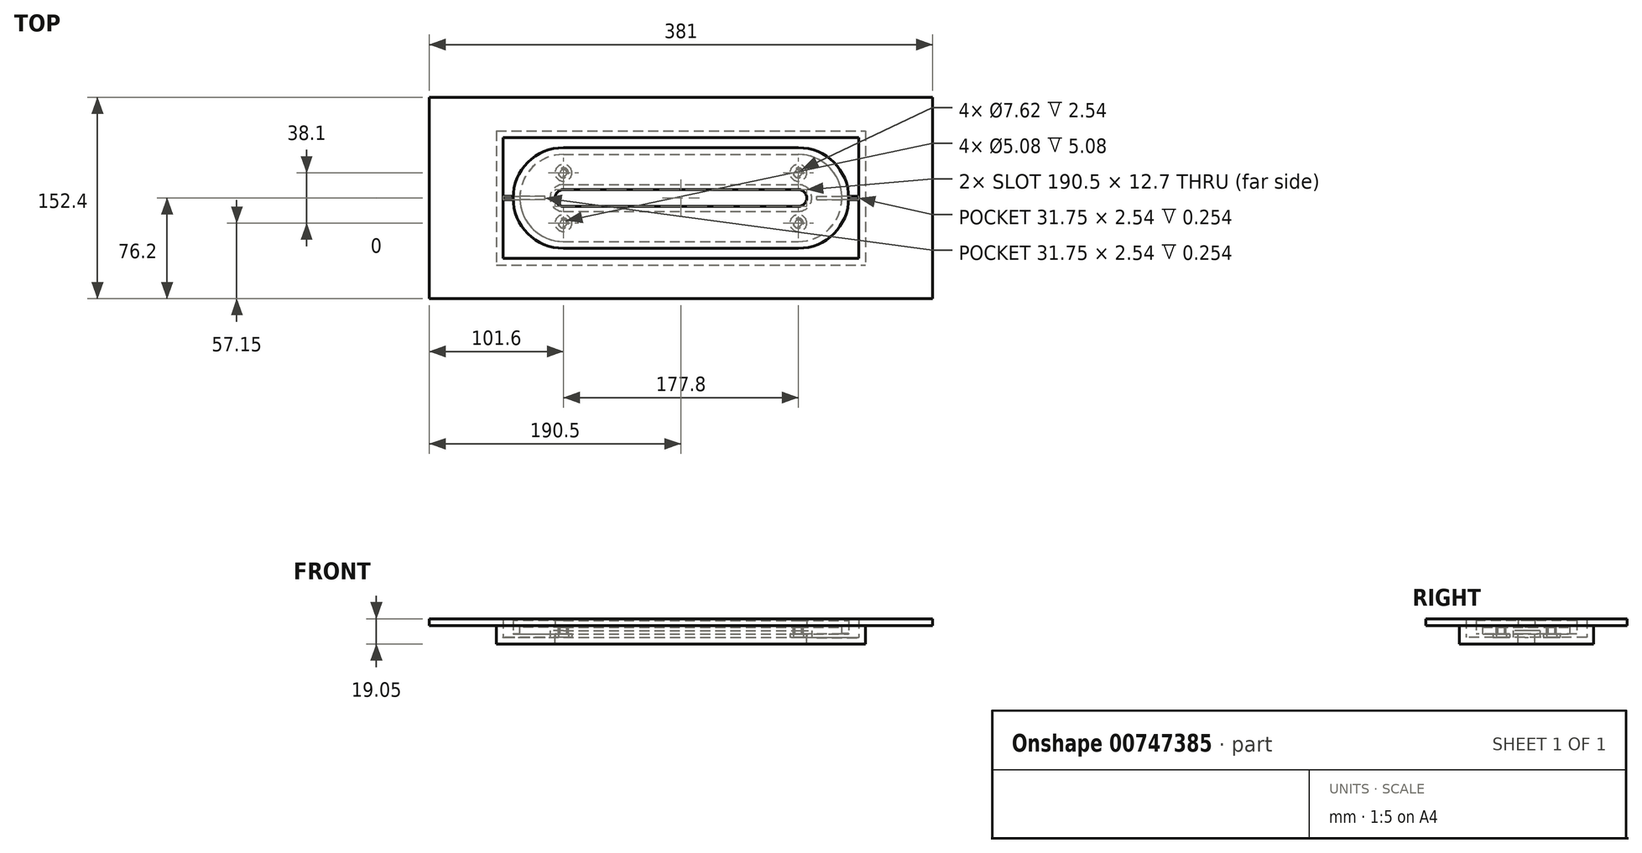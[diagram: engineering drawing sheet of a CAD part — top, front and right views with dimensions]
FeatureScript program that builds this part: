
annotation { "Feature Type Name" : "Feature", "Feature Type Description" : "" }
export const myFeature = defineFeature(function(context is Context, id is Id, definition is map)
    precondition{}
    {
        {
            var Q0;
            Q0=qCreatedBy(makeId("Top.planeOp"),FACE);
            var sketch = newSketch(context, id + "F0", { "sketchPlane" : qUnion([Q0])});
            skLineSegment(sketch, "E0.bottom", {"start": v(-139.7, 50.8) * mm, "end": v(139.7, 50.8) * mm});
            skLineSegment(sketch, "E0.top", {"start": v(-139.7, -50.8) * mm, "end": v(139.7, -50.8) * mm});
            skLineSegment(sketch, "E0.left", {"start": v(-139.7, 50.8) * mm, "end": v(-139.7, -50.8) * mm});
            skLineSegment(sketch, "E0.right", {"start": v(139.7, 50.8) * mm, "end": v(139.7, -50.8) * mm});
            skPoint(sketch, "E0.middle", {"position": v(0, 0) * mm});
            skSolve(sketch);
        }
        {
            var Q0;
            Q0=qSketchRegion(id+"F0",true);
            extrude(context, id + "F1", {"entities" : qUnion([Q0]), "depth" : 5.08 * mm, "offsetDistance" : 25.4 * mm});
        }
        {
            var Q0;
            Q0=makeQuery(id+"F1.opExtrude","CAP_FACE",FACE,{"disambiguationData":[OSD([sQuery(id+"F0.wireOp",EDGE,"E0.bottom"),sQuery(id+"F0.wireOp",EDGE,"E0.top"),sQuery(id+"F0.wireOp",EDGE,"E0.left"),sQuery(id+"F0.wireOp",EDGE,"E0.right")])],"isStart":false});
            var sketch = newSketch(context, id + "F2", { "sketchPlane" : qUnion([Q0])});
            skLineSegment(sketch, "E1", {"start": v(-139.7, 0) * mm, "end": v(139.7, 0) * mm, "construction": true});
            skLineSegment(sketch, "E2.bottom", {"start": v(-88.9, -6.35) * mm, "end": v(88.9, -6.35) * mm});
            skLineSegment(sketch, "E2.top", {"start": v(-88.9, 6.35) * mm, "end": v(88.9, 6.35) * mm});
            skLineSegment(sketch, "E2.left", {"start": v(-88.9, -6.35) * mm, "end": v(-88.9, 6.35) * mm, "construction": true});
            skLineSegment(sketch, "E2.right", {"start": v(88.9, -6.35) * mm, "end": v(88.9, 6.35) * mm, "construction": true});
            skPoint(sketch, "E2.middle", {"position": v(0, 0) * mm});
            skArc(sketch, "E3", {"start": v(-88.9, 6.35) * mm, "mid": v(-95.25, 0) * mm, "end": v(-88.9, -6.35) * mm});
            skArc(sketch, "E4", {"start": v(88.9, -6.35) * mm, "mid": v(95.25, 0) * mm, "end": v(88.9, 6.35) * mm});
            skSolve(sketch);
        }
        {
            var Q0;
            Q0=qSketchRegion(id+"F2",true);
            extrude(context, id + "F3", {"entities" : qUnion([Q0]), "operationType" : NewBodyOperationType.REMOVE, "endBound" : BoundingType.THROUGH_ALL, "oppositeDirection" : true, "depth" : 25.4 * mm, "offsetDistance" : 25.4 * mm});
        }
        {
            var Q0;
            Q0=makeQuery(id+"F1.opExtrude","CAP_FACE",FACE,{"disambiguationData":[OSD([sQuery(id+"F0.wireOp",EDGE,"E0.bottom"),sQuery(id+"F0.wireOp",EDGE,"E0.top"),sQuery(id+"F0.wireOp",EDGE,"E0.left"),sQuery(id+"F0.wireOp",EDGE,"E0.right")])],"isStart":false});
            var sketch = newSketch(context, id + "F4", { "sketchPlane" : qUnion([Q0])});
            skLineSegment(sketch, "E5", {"start": v(-139.7, 0) * mm, "end": v(139.7, 0) * mm, "construction": true});
            skLineSegment(sketch, "E6.bottom", {"start": v(-88.9, 6.35) * mm, "end": v(88.9, 6.35) * mm});
            skLineSegment(sketch, "E6.top", {"start": v(-88.9, -6.35) * mm, "end": v(88.9, -6.35) * mm});
            skLineSegment(sketch, "E6.left", {"start": v(-88.9, 6.35) * mm, "end": v(-88.9, -6.35) * mm, "construction": true});
            skLineSegment(sketch, "E6.right", {"start": v(88.9, 6.35) * mm, "end": v(88.9, -6.35) * mm, "construction": true});
            skPoint(sketch, "E6.middle", {"position": v(0, 0) * mm});
            skArc(sketch, "E7", {"start": v(-88.9, 6.35) * mm, "mid": v(-95.25, 0) * mm, "end": v(-88.9, -6.35) * mm});
            skArc(sketch, "E8", {"start": v(88.9, -6.35) * mm, "mid": v(95.25, 0) * mm, "end": v(88.9, 6.35) * mm});
            skLineSegment(sketch, "E9.0", {"start": v(-88.9, 10.16) * mm, "end": v(88.9, 10.16) * mm});
            skArc(sketch, "E9.1", {"start": v(-88.9, 10.16) * mm, "mid": v(-99.06, 0) * mm, "end": v(-88.9, -10.16) * mm});
            skLineSegment(sketch, "E9.2", {"start": v(-88.9, -10.16) * mm, "end": v(88.9, -10.16) * mm});
            skArc(sketch, "E9.3", {"start": v(88.9, -10.16) * mm, "mid": v(99.06, 0) * mm, "end": v(88.9, 10.16) * mm});
            skSolve(sketch);
        }
        {
            var Q0;
            Q0=qSketchRegion(id+"F4",true);
            extrude(context, id + "F5", {"entities" : qUnion([Q0]), "operationType" : NewBodyOperationType.ADD, "depth" : 5.08 * mm, "offsetDistance" : 25.4 * mm});
        }
        {
            var Q0;
            Q0=qCreatedBy(makeId("Top.planeOp"),FACE);
            cPlane(context, id + "F6", {"entities" : qUnion([Q0]), "cplaneType" : CPlaneType.OFFSET, "offset" : 12.7 * mm, "width" : 152.4 * mm, "height" : 152.4 * mm});
        }
        {
            var Q0;
            Q0=qCreatedBy(id+"F6.planeOp",FACE);
            var sketch = newSketch(context, id + "F7", { "sketchPlane" : qUnion([Q0])});
            skLineSegment(sketch, "E10.bottom", {"start": v(-88.9, 38.1) * mm, "end": v(88.9, 38.1) * mm});
            skLineSegment(sketch, "E10.top", {"start": v(-88.9, -38.1) * mm, "end": v(88.9, -38.1) * mm});
            skLineSegment(sketch, "E10.left", {"start": v(-88.9, 38.1) * mm, "end": v(-88.9, -38.1) * mm, "construction": true});
            skLineSegment(sketch, "E10.right", {"start": v(88.9, 38.1) * mm, "end": v(88.9, -38.1) * mm, "construction": true});
            skPoint(sketch, "E10.middle", {"position": v(0, 0) * mm});
            skLineSegment(sketch, "E11", {"start": v(-88.9, 0) * mm, "end": v(88.9, 0) * mm, "construction": true});
            skArc(sketch, "E12", {"start": v(-88.9, 38.1) * mm, "mid": v(-127, 0) * mm, "end": v(-88.9, -38.1) * mm});
            skArc(sketch, "E13", {"start": v(88.9, -38.1) * mm, "mid": v(127, 0) * mm, "end": v(88.9, 38.1) * mm});
            skLineSegment(sketch, "E14", {"start": v(-88.9, 6.35) * mm, "end": v(88.9, 6.35) * mm});
            skLineSegment(sketch, "E15", {"start": v(-88.9, -6.35) * mm, "end": v(88.9, -6.35) * mm});
            skLineSegment(sketch, "E16", {"start": v(0, 6.35) * mm, "end": v(0, -6.35) * mm, "construction": true});
            skArc(sketch, "E17", {"start": v(-88.9, 6.35) * mm, "mid": v(-95.25, 0) * mm, "end": v(-88.9, -6.35) * mm});
            skArc(sketch, "E18", {"start": v(88.9, -6.35) * mm, "mid": v(95.25, 0) * mm, "end": v(88.9, 6.35) * mm});
            skSolve(sketch);
        }
        {
            var Q0;
            Q0=makeQuery(id+"F7.imprint","IMPRINT",FACE,{"disambiguationData":[TD([[makeQuery(id+"F7.imprint","IMPRINT",EDGE,{"derivedFrom":sQuery(id+"F7.wireOp",EDGE,"E10.bottom")}),-1.0]])]});
            extrude(context, id + "F8", {"entities" : qUnion([Q0]), "depth" : 5.08 * mm, "offsetDistance" : 25.4 * mm});
        }
        {
            var Q0;
            Q0=makeQuery(id+"F8.opExtrude","CAP_FACE",FACE,{"disambiguationData":[OSD([sQuery(id+"F7.wireOp",EDGE,"E10.bottom"),sQuery(id+"F7.wireOp",EDGE,"E10.top"),sQuery(id+"F7.wireOp",EDGE,"E12"),sQuery(id+"F7.wireOp",EDGE,"E13"),sQuery(id+"F7.wireOp",EDGE,"E14"),sQuery(id+"F7.wireOp",EDGE,"E15"),sQuery(id+"F7.wireOp",EDGE,"E17"),sQuery(id+"F7.wireOp",EDGE,"E18")])],"isStart":true});
            var sketch = newSketch(context, id + "F9", { "sketchPlane" : qUnion([Q0])});
            skLineSegment(sketch, "E19.bottom", {"start": v(-88.9, 38.1) * mm, "end": v(88.9, 38.1) * mm});
            skLineSegment(sketch, "E19.top", {"start": v(-88.9, -38.1) * mm, "end": v(88.9, -38.1) * mm});
            skLineSegment(sketch, "E19.left", {"start": v(-88.9, 38.1) * mm, "end": v(-88.9, -38.1) * mm, "construction": true});
            skLineSegment(sketch, "E19.right", {"start": v(88.9, 38.1) * mm, "end": v(88.9, -38.1) * mm, "construction": true});
            skPoint(sketch, "E19.middle", {"position": v(0, 0) * mm});
            skArc(sketch, "E20", {"start": v(-88.9, 38.1) * mm, "mid": v(-127, 0) * mm, "end": v(-88.9, -38.1) * mm});
            skArc(sketch, "E21", {"start": v(88.9, -38.1) * mm, "mid": v(127, 0) * mm, "end": v(88.9, 38.1) * mm});
            skArc(sketch, "E22.0", {"start": v(-88.9, 33.02) * mm, "mid": v(-121.92, 0) * mm, "end": v(-88.9, -33.02) * mm});
            skLineSegment(sketch, "E22.1", {"start": v(-88.9, 33.02) * mm, "end": v(88.9, 33.02) * mm});
            skArc(sketch, "E22.2", {"start": v(88.9, -33.02) * mm, "mid": v(121.92, 0) * mm, "end": v(88.9, 33.02) * mm});
            skLineSegment(sketch, "E22.3", {"start": v(-88.9, -33.02) * mm, "end": v(88.9, -33.02) * mm});
            skSolve(sketch);
        }
        {
            var Q0;
            Q0=makeQuery(id+"F9.imprint","IMPRINT",FACE,{"disambiguationData":[TD([[makeQuery(id+"F9.imprint","IMPRINT",EDGE,{"derivedFrom":sQuery(id+"F9.wireOp",EDGE,"E19.bottom")}),-1.0]])]});
            extrude(context, id + "F10", {"entities" : qUnion([Q0]), "operationType" : NewBodyOperationType.ADD, "depth" : 5.08 * mm, "offsetDistance" : 25.4 * mm});
        }
        {
            var Q0;
            Q0=makeQuery(id+"F1.opExtrude","CAP_FACE",FACE,{"disambiguationData":[OSD([sQuery(id+"F0.wireOp",EDGE,"E0.bottom"),sQuery(id+"F0.wireOp",EDGE,"E0.top"),sQuery(id+"F0.wireOp",EDGE,"E0.left"),sQuery(id+"F0.wireOp",EDGE,"E0.right")])],"isStart":false});
            var sketch = newSketch(context, id + "F11", { "sketchPlane" : qUnion([Q0])});
            skLineSegment(sketch, "E23", {"start": v(-139.7, 0) * mm, "end": v(139.7, 0) * mm, "construction": true});
            skLineSegment(sketch, "E24", {"start": v(0, 50.8) * mm, "end": v(0, -50.8) * mm, "construction": true});
            skCircle(sketch, "E25", {"center": v(-88.9, -19.05) * mm, "radius": 6.35 * mm});
            skCircle(sketch, "E26", {"center": v(-88.9, -19.05) * mm, "radius": 3.81 * mm});
            skCircle(sketch, "E27.MirrorC", {"center": v(-88.9, 19.05) * mm, "radius": 3.81 * mm});
            skCircle(sketch, "E28.MirrorC", {"center": v(-88.9, 19.05) * mm, "radius": 6.35 * mm});
            skCircle(sketch, "E29.MirrorC", {"center": v(88.9, -19.05) * mm, "radius": 3.81 * mm});
            skCircle(sketch, "E30.MirrorC", {"center": v(88.9, 19.05) * mm, "radius": 3.81 * mm});
            skCircle(sketch, "E31.MirrorC", {"center": v(88.9, -19.05) * mm, "radius": 6.35 * mm});
            skCircle(sketch, "E32.MirrorC", {"center": v(88.9, 19.05) * mm, "radius": 6.35 * mm});
            skSolve(sketch);
        }
        {
            var Q0;
            Q0=qSketchRegion(id+"F11",true);
            extrude(context, id + "F12", {"entities" : qUnion([Q0]), "operationType" : NewBodyOperationType.ADD, "depth" : 2.54 * mm, "offsetDistance" : 25.4 * mm});
        }
        {
            var Q0;
            Q0=makeQuery(id+"F8.opExtrude","CAP_FACE",FACE,{"disambiguationData":[OSD([sQuery(id+"F7.wireOp",EDGE,"E10.bottom"),sQuery(id+"F7.wireOp",EDGE,"E10.top"),sQuery(id+"F7.wireOp",EDGE,"E12"),sQuery(id+"F7.wireOp",EDGE,"E13"),sQuery(id+"F7.wireOp",EDGE,"E14"),sQuery(id+"F7.wireOp",EDGE,"E15"),sQuery(id+"F7.wireOp",EDGE,"E17"),sQuery(id+"F7.wireOp",EDGE,"E18")])],"isStart":true});
            var sketch = newSketch(context, id + "F13", { "sketchPlane" : qUnion([Q0])});
            skLineSegment(sketch, "E33", {"start": v(-121.92, 0) * mm, "end": v(121.92, 0) * mm, "construction": true});
            skLineSegment(sketch, "E34", {"start": v(0, 33.02) * mm, "end": v(0, -33.02) * mm, "construction": true});
            skCircle(sketch, "E35", {"center": v(-88.9, -19.05) * mm, "radius": 3.68 * mm});
            skCircle(sketch, "E36", {"center": v(-88.9, -19.05) * mm, "radius": 2.54 * mm});
            skCircle(sketch, "E37.MirrorC", {"center": v(-88.9, 19.05) * mm, "radius": 2.54 * mm});
            skCircle(sketch, "E38.MirrorC", {"center": v(-88.9, 19.05) * mm, "radius": 3.68 * mm});
            skCircle(sketch, "E39.MirrorC", {"center": v(88.9, -19.05) * mm, "radius": 3.68 * mm});
            skCircle(sketch, "E40.MirrorC", {"center": v(88.9, 19.05) * mm, "radius": 3.68 * mm});
            skCircle(sketch, "E41.MirrorC", {"center": v(88.9, 19.05) * mm, "radius": 2.54 * mm});
            skCircle(sketch, "E42.MirrorC", {"center": v(88.9, -19.05) * mm, "radius": 2.54 * mm});
            skSolve(sketch);
        }
        {
            var Q0;
            Q0=qSketchRegion(id+"F13",true);
            extrude(context, id + "F14", {"entities" : qUnion([Q0]), "operationType" : NewBodyOperationType.ADD, "depth" : 5.08 * mm, "offsetDistance" : 25.4 * mm});
        }
        {
            var Q0;
            {var subQ0=sQuery(id+"F0.wireOp",EDGE,"E0.bottom");var subQ1=sQuery(id+"F0.wireOp",EDGE,"E0.right");var subQ2=sQuery(id+"F0.wireOp",EDGE,"E0.top");var subQ3=sQuery(id+"F0.wireOp",EDGE,"E0.left");Q0=makeQuery(id+"F12.boolean.opBoolean","SPLIT",FACE,{"disambiguationData":[TD([makeQuery(id+"F1.opExtrude","SWEPT_FACE",FACE,{"disambiguationData":[OSD([subQ0])]})])],"derivedFrom":makeQuery(id+"F1.opExtrude","CAP_FACE",FACE,{"disambiguationData":[OSD([subQ0,subQ2,subQ3,subQ1])],"isStart":false})});}
            var sketch = newSketch(context, id + "F15", { "sketchPlane" : qUnion([Q0])});
            skLineSegment(sketch, "E43.bottom", {"start": v(-139.7, 50.8) * mm, "end": v(139.7, 50.8) * mm});
            skLineSegment(sketch, "E43.top", {"start": v(-139.7, -50.8) * mm, "end": v(139.7, -50.8) * mm});
            skLineSegment(sketch, "E43.left", {"start": v(-139.7, 50.8) * mm, "end": v(-139.7, -50.8) * mm});
            skLineSegment(sketch, "E43.right", {"start": v(139.7, 50.8) * mm, "end": v(139.7, -50.8) * mm});
            skLineSegment(sketch, "E44.0", {"start": v(-134.62, 45.72) * mm, "end": v(134.62, 45.72) * mm});
            skLineSegment(sketch, "E44.1", {"start": v(-134.62, 45.72) * mm, "end": v(-134.62, -45.72) * mm});
            skLineSegment(sketch, "E44.2", {"start": v(-134.62, -45.72) * mm, "end": v(134.62, -45.72) * mm});
            skLineSegment(sketch, "E44.3", {"start": v(134.62, 45.72) * mm, "end": v(134.62, -45.72) * mm});
            skSolve(sketch);
        }
        {
            var Q0;
            Q0 = qSketchRegion(id + "F15", true);
            extrude(context, id + "F16", {"entities" : qUnion([Q0]), "operationType" : NewBodyOperationType.ADD, "depth" : 13.97 * mm, "offsetDistance" : 25.4 * mm});
        }
        {
            var Q0;
            {var subQ0=sQuery(id+"F0.wireOp",EDGE,"E0.bottom");var subQ1=sQuery(id+"F0.wireOp",EDGE,"E0.right");var subQ2=sQuery(id+"F0.wireOp",EDGE,"E0.top");var subQ3=sQuery(id+"F0.wireOp",EDGE,"E0.left");Q0=makeQuery(id+"F12.boolean.opBoolean","SPLIT",FACE,{"disambiguationData":[TD([makeQuery(id+"F1.opExtrude","SWEPT_FACE",FACE,{"disambiguationData":[OSD([subQ0])]})])],"derivedFrom":makeQuery(id+"F1.opExtrude","CAP_FACE",FACE,{"disambiguationData":[OSD([subQ0,subQ2,subQ3,subQ1])],"isStart":false})});}
            var sketch = newSketch(context, id + "F17", { "sketchPlane" : qUnion([Q0])});
            skLineSegment(sketch, "E45", {"start": v(-134.62, 0) * mm, "end": v(134.62, 0) * mm, "construction": true});
            skLineSegment(sketch, "E46", {"start": v(0, 45.72) * mm, "end": v(0, -45.72) * mm, "construction": true});
            skLineSegment(sketch, "E47.bottom", {"start": v(-102.87, -1.27) * mm, "end": v(-134.62, -1.27) * mm});
            skLineSegment(sketch, "E47.top", {"start": v(-102.87, 1.27) * mm, "end": v(-134.62, 1.27) * mm});
            skLineSegment(sketch, "E47.left", {"start": v(-102.87, -1.27) * mm, "end": v(-102.87, 1.27) * mm});
            skLineSegment(sketch, "E47.right", {"start": v(-134.62, -1.27) * mm, "end": v(-134.62, 1.27) * mm});
            skPoint(sketch, "E47.middle", {"position": v(-118.75, 0) * mm});
            skLineSegment(sketch, "E48.MirrorCS", {"start": v(134.62, -1.27) * mm, "end": v(134.62, 1.27) * mm});
            skLineSegment(sketch, "E49.MirrorCS", {"start": v(102.87, -1.27) * mm, "end": v(102.87, 1.27) * mm});
            skPoint(sketch, "E50.MirrorP", {"position": v(118.75, 0) * mm});
            skLineSegment(sketch, "E51.MirrorCS", {"start": v(102.87, -1.27) * mm, "end": v(134.62, -1.27) * mm});
            skLineSegment(sketch, "E52.MirrorCS", {"start": v(102.87, 1.27) * mm, "end": v(134.62, 1.27) * mm});
            skSolve(sketch);
        }
        {
            var Q0;
            Q0=qSketchRegion(id+"F17",true);
            extrude(context, id + "F18", {"entities" : qUnion([Q0]), "operationType" : NewBodyOperationType.REMOVE, "oppositeDirection" : true, "depth" : 0.25 * mm, "offsetDistance" : 25.4 * mm});
        }
        {
            var Q0;
            Q0=makeQuery(id+"F10.opExtrude","CAP_FACE",FACE,{"disambiguationData":[OSD([sQuery(id+"F9.wireOp",EDGE,"E19.bottom"),sQuery(id+"F9.wireOp",EDGE,"E19.top"),sQuery(id+"F9.wireOp",EDGE,"E20"),sQuery(id+"F9.wireOp",EDGE,"E21"),sQuery(id+"F9.wireOp",EDGE,"E22.0"),sQuery(id+"F9.wireOp",EDGE,"E22.1"),sQuery(id+"F9.wireOp",EDGE,"E22.2"),sQuery(id+"F9.wireOp",EDGE,"E22.3")])],"isStart":false});
            var sketch = newSketch(context, id + "F19", { "sketchPlane" : qUnion([Q0])});
            skLineSegment(sketch, "E53", {"start": v(-127, 0) * mm, "end": v(127, 0) * mm, "construction": true});
            skLineSegment(sketch, "E54", {"start": v(0, 38.1) * mm, "end": v(0, -38.1) * mm, "construction": true});
            skLineSegment(sketch, "E55.bottom", {"start": v(-127.63, 1.27) * mm, "end": v(-121.28, 1.27) * mm});
            skLineSegment(sketch, "E55.top", {"start": v(-127.63, -1.27) * mm, "end": v(-121.28, -1.27) * mm});
            skLineSegment(sketch, "E55.left", {"start": v(-127.63, 1.27) * mm, "end": v(-127.63, -1.27) * mm});
            skLineSegment(sketch, "E55.right", {"start": v(-121.28, 1.27) * mm, "end": v(-121.28, -1.27) * mm});
            skPoint(sketch, "E55.middle", {"position": v(-124.46, 0) * mm});
            skLineSegment(sketch, "E56.MirrorCS", {"start": v(121.28, 1.27) * mm, "end": v(121.28, -1.27) * mm});
            skLineSegment(sketch, "E57.MirrorCS", {"start": v(127.63, 1.27) * mm, "end": v(127.63, -1.27) * mm});
            skLineSegment(sketch, "E58.MirrorCS", {"start": v(127.63, 1.27) * mm, "end": v(121.28, 1.27) * mm});
            skLineSegment(sketch, "E59.MirrorCS", {"start": v(127.63, -1.27) * mm, "end": v(121.28, -1.27) * mm});
            skPoint(sketch, "E60.MirrorP", {"position": v(124.46, 0) * mm});
            skSolve(sketch);
        }
        {
            var Q0;
            Q0=qSketchRegion(id+"F19",true);
            extrude(context, id + "F20", {"entities" : qUnion([Q0]), "operationType" : NewBodyOperationType.REMOVE, "oppositeDirection" : true, "depth" : 0.25 * mm, "offsetDistance" : 25.4 * mm});
        }
        {
            var Q0;
            Q0=makeQuery(id+"F16.opExtrude","CAP_FACE",FACE,{"disambiguationData":[OSD([sQuery(id+"F15.wireOp",EDGE,"E43.bottom"),sQuery(id+"F15.wireOp",EDGE,"E43.top"),sQuery(id+"F15.wireOp",EDGE,"E43.left"),sQuery(id+"F15.wireOp",EDGE,"E43.right"),sQuery(id+"F15.wireOp",EDGE,"E44.0"),sQuery(id+"F15.wireOp",EDGE,"E44.1"),sQuery(id+"F15.wireOp",EDGE,"E44.2"),sQuery(id+"F15.wireOp",EDGE,"E44.3")])],"isStart":false});
            var sketch = newSketch(context, id + "F21", { "sketchPlane" : qUnion([Q0])});
            skLineSegment(sketch, "E61.bottom", {"start": v(-139.7, 50.8) * mm, "end": v(139.7, 50.8) * mm});
            skLineSegment(sketch, "E61.top", {"start": v(-139.7, -50.8) * mm, "end": v(139.7, -50.8) * mm});
            skLineSegment(sketch, "E61.left", {"start": v(-139.7, 50.8) * mm, "end": v(-139.7, -50.8) * mm});
            skLineSegment(sketch, "E61.right", {"start": v(139.7, 50.8) * mm, "end": v(139.7, -50.8) * mm});
            skLineSegment(sketch, "E62.bottom", {"start": v(-190.5, 76.2) * mm, "end": v(190.5, 76.2) * mm});
            skLineSegment(sketch, "E62.top", {"start": v(-190.5, -76.2) * mm, "end": v(190.5, -76.2) * mm});
            skLineSegment(sketch, "E62.left", {"start": v(-190.5, 76.2) * mm, "end": v(-190.5, -76.2) * mm});
            skLineSegment(sketch, "E62.right", {"start": v(190.5, 76.2) * mm, "end": v(190.5, -76.2) * mm});
            skPoint(sketch, "E62.middle", {"position": v(0, 0) * mm});
            skSolve(sketch);
        }
        {
            var Q0;
            Q0 = qSketchRegion(id + "F21", true);
            extrude(context, id + "F22", {"entities" : qUnion([Q0]), "operationType" : NewBodyOperationType.ADD, "oppositeDirection" : true, "depth" : 5.08 * mm, "offsetDistance" : 25.4 * mm});
        }
    });
